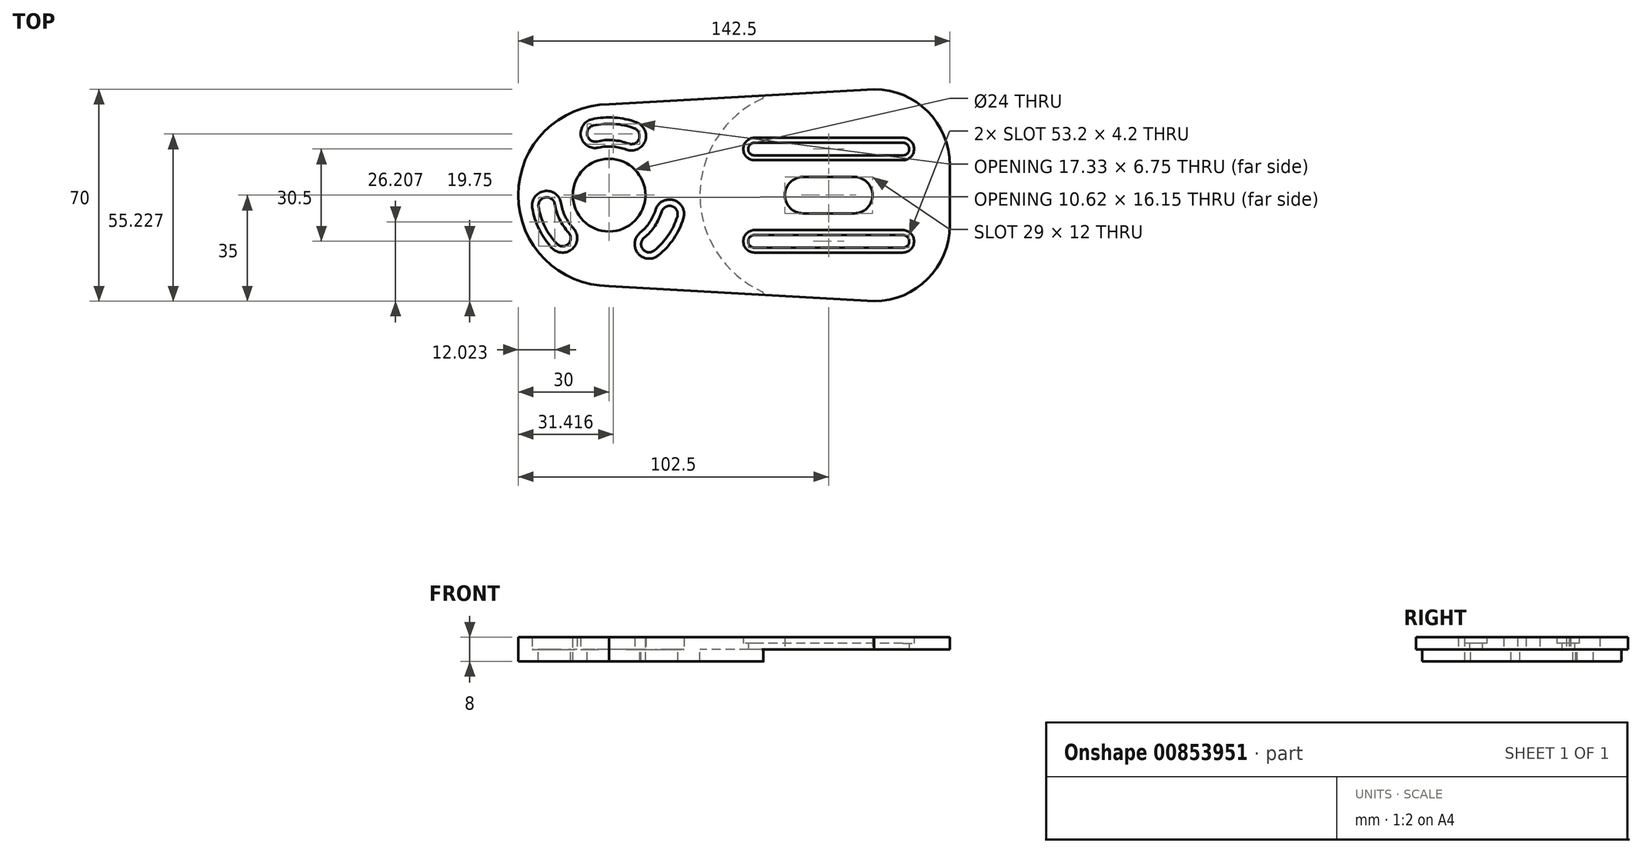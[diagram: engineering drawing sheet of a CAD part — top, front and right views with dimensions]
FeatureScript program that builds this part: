
annotation { "Feature Type Name" : "Feature", "Feature Type Description" : "" }
export const myFeature = defineFeature(function(context is Context, id is Id, definition is map)
    precondition{}
    {
        {
            var Q0;
            Q0=qCreatedBy(makeId("Top.planeOp"),FACE);
            var sketch = newSketch(context, id + "F0", { "sketchPlane" : qUnion([Q0])});
            skLineSegment(sketch, "E0.bottom", {"start": v(39.15, 35) * mm, "end": v(-48.35, 35) * mm, "construction": true});
            skLineSegment(sketch, "E0.top", {"start": v(39.15, -35) * mm, "end": v(-48.35, -35) * mm, "construction": true});
            skLineSegment(sketch, "E0.left", {"start": v(64.15, 10) * mm, "end": v(64.15, -10) * mm});
            skCircle(sketch, "E1", {"center": v(-48.35, 0) * mm, "radius": 12 * mm});
            skArc(sketch, "E2.filletArc", {"start": v(64.15, 10) * mm, "mid": v(56.83, 27.68) * mm, "end": v(39.15, 35) * mm});
            skArc(sketch, "E3.filletArc", {"start": v(39.15, -35) * mm, "mid": v(56.83, -27.68) * mm, "end": v(64.15, -10) * mm});
            skLineSegment(sketch, "E4.bottom", {"start": v(32.65, 6) * mm, "end": v(24.15, 6) * mm});
            skPoint(sketch, "E4.middle", {"position": v(24.15, 0) * mm});
            skLineSegment(sketch, "E5", {"start": v(-48.35, 0) * mm, "end": v(-47.08, 18.16) * mm, "construction": true});
            skPoint(sketch, "E6", {"position": v(64.15, 0) * mm});
            skArc(sketch, "E7", {"start": v(-54, 25.07) * mm, "mid": v(-57.62, 19.34) * mm, "end": v(-51.88, 15.7) * mm});
            skArc(sketch, "E8", {"start": v(-53.53, 23.02) * mm, "mid": v(-55.57, 19.8) * mm, "end": v(-52.35, 17.76) * mm});
            skArc(sketch, "E9", {"start": v(-41.92, 17.03) * mm, "mid": v(-38.44, 18.6) * mm, "end": v(-40.01, 22.08) * mm});
            skArc(sketch, "E10.trimOffspring", {"start": v(-42.66, 15.06) * mm, "mid": v(-47.23, 16.06) * mm, "end": v(-51.88, 15.7) * mm});
            skArc(sketch, "E11.trimOffspring", {"start": v(-41.92, 17.03) * mm, "mid": v(-47.08, 18.16) * mm, "end": v(-52.35, 17.76) * mm});
            skArc(sketch, "E12.trimOffspring", {"start": v(-40.01, 22.08) * mm, "mid": v(-46.7, 23.54) * mm, "end": v(-53.53, 23.02) * mm});
            skArc(sketch, "E13.trimOffspring", {"start": v(-39.27, 24.04) * mm, "mid": v(-46.56, 25.64) * mm, "end": v(-54, 25.07) * mm});
            skArc(sketch, "E14.trimOffspring", {"start": v(-42.66, 15.06) * mm, "mid": v(-36.48, 17.86) * mm, "end": v(-39.27, 24.04) * mm});
            skCircle(sketch, "E15", {"center": v(-48.35, 0) * mm, "radius": 20.9 * mm, "construction": true});
            skLineSegment(sketch, "E16", {"start": v(32.65, 0) * mm, "end": v(24.15, 0) * mm, "construction": true});
            skArc(sketch, "E17", {"start": v(32.65, -6) * mm, "mid": v(38.65, 0) * mm, "end": v(32.65, 6) * mm});
            skLineSegment(sketch, "E18", {"start": v(24.15, 0) * mm, "end": v(24.15, 6) * mm, "construction": true});
            skLineSegment(sketch, "E19.MirrorCS", {"start": v(32.65, -6) * mm, "end": v(24.15, -6) * mm});
            skLineSegment(sketch, "E20.MirrorCS", {"start": v(15.65, 6) * mm, "end": v(24.15, 6) * mm});
            skArc(sketch, "E21.MirrorCS", {"start": v(15.65, -6) * mm, "mid": v(9.65, 0) * mm, "end": v(15.65, 6) * mm});
            skLineSegment(sketch, "E22.MirrorCS", {"start": v(15.65, -6) * mm, "end": v(24.15, -6) * mm});
            skArc(sketch, "E23", {"start": v(-0.35, -11.55) * mm, "mid": v(-4.05, -15.25) * mm, "end": v(-0.35, -18.95) * mm});
            skArc(sketch, "E24", {"start": v(-0.35, -13.15) * mm, "mid": v(-2.45, -15.25) * mm, "end": v(-0.35, -17.35) * mm});
            skLineSegment(sketch, "E25", {"start": v(-0.35, -11.55) * mm, "end": v(24.15, -11.55) * mm});
            skLineSegment(sketch, "E26", {"start": v(-0.35, -15.25) * mm, "end": v(24.15, -15.25) * mm, "construction": true});
            skLineSegment(sketch, "E27", {"start": v(-0.35, -13.15) * mm, "end": v(24.15, -13.15) * mm});
            skLineSegment(sketch, "E28.MirrorCS", {"start": v(-0.35, -17.35) * mm, "end": v(24.15, -17.35) * mm});
            skLineSegment(sketch, "E29.MirrorCS", {"start": v(-0.35, -18.95) * mm, "end": v(24.15, -18.95) * mm});
            skLineSegment(sketch, "E30.MirrorCS", {"start": v(48.65, -11.55) * mm, "end": v(24.15, -11.55) * mm});
            skLineSegment(sketch, "E31.MirrorCS", {"start": v(48.65, -13.15) * mm, "end": v(24.15, -13.15) * mm});
            skLineSegment(sketch, "E32.MirrorCS", {"start": v(48.65, -17.35) * mm, "end": v(24.15, -17.35) * mm});
            skLineSegment(sketch, "E33.MirrorCS", {"start": v(48.65, -18.95) * mm, "end": v(24.15, -18.95) * mm});
            skArc(sketch, "E34.MirrorCS", {"start": v(48.65, -13.15) * mm, "mid": v(50.75, -15.25) * mm, "end": v(48.65, -17.35) * mm});
            skArc(sketch, "E35.MirrorCS", {"start": v(48.65, -11.55) * mm, "mid": v(52.35, -15.25) * mm, "end": v(48.65, -18.95) * mm});
            skLineSegment(sketch, "E36.MirrorCS", {"start": v(-0.35, 11.55) * mm, "end": v(24.15, 11.55) * mm});
            skArc(sketch, "E37.MirrorCS", {"start": v(-0.35, 11.55) * mm, "mid": v(-4.05, 15.25) * mm, "end": v(-0.35, 18.95) * mm});
            skArc(sketch, "E38.MirrorCS", {"start": v(-0.35, 13.15) * mm, "mid": v(-2.45, 15.25) * mm, "end": v(-0.35, 17.35) * mm});
            skLineSegment(sketch, "E39.MirrorCS", {"start": v(-0.35, 13.15) * mm, "end": v(24.15, 13.15) * mm});
            skLineSegment(sketch, "E40.MirrorCS", {"start": v(-0.35, 17.35) * mm, "end": v(24.15, 17.35) * mm});
            skLineSegment(sketch, "E41.MirrorCS", {"start": v(-0.35, 18.95) * mm, "end": v(24.15, 18.95) * mm});
            skLineSegment(sketch, "E42.MirrorCS", {"start": v(48.65, 18.95) * mm, "end": v(24.15, 18.95) * mm});
            skLineSegment(sketch, "E43.MirrorCS", {"start": v(48.65, 17.35) * mm, "end": v(24.15, 17.35) * mm});
            skLineSegment(sketch, "E44.MirrorCS", {"start": v(48.65, 13.15) * mm, "end": v(24.15, 13.15) * mm});
            skLineSegment(sketch, "E45.MirrorCS", {"start": v(48.65, 11.55) * mm, "end": v(24.15, 11.55) * mm});
            skArc(sketch, "E46.MirrorCS", {"start": v(48.65, 11.55) * mm, "mid": v(52.35, 15.25) * mm, "end": v(48.65, 18.95) * mm});
            skArc(sketch, "E47.MirrorCS", {"start": v(48.65, 13.15) * mm, "mid": v(50.75, 15.25) * mm, "end": v(48.65, 17.35) * mm});
            skLineSegment(sketch, "E48", {"start": v(-48.35, 0) * mm, "end": v(-48.35, -30) * mm, "construction": true});
            skLineSegment(sketch, "E49.MirrorCS", {"start": v(-48.35, 0) * mm, "end": v(-48.35, 30) * mm, "construction": true});
            skLineSegment(sketch, "E50", {"start": v(39.15, 35) * mm, "end": v(-48.35, 30) * mm});
            skLineSegment(sketch, "E51", {"start": v(39.15, -35) * mm, "end": v(-48.35, -30) * mm});
            skArc(sketch, "E52", {"start": v(-48.35, 30) * mm, "mid": v(-78.35, 0) * mm, "end": v(-48.35, -30) * mm});
            skArc(sketch, "E53.1.0", {"start": v(-73.71, -4.16) * mm, "mid": v(-71.45, -11.27) * mm, "end": v(-67.24, -17.42) * mm});
            skArc(sketch, "E53.1.1", {"start": v(-67.24, -17.42) * mm, "mid": v(-60.46, -17.7) * mm, "end": v(-60.19, -10.92) * mm});
            skArc(sketch, "E53.1.2", {"start": v(-65.7, -16) * mm, "mid": v(-61.88, -16.15) * mm, "end": v(-61.73, -12.34) * mm});
            skArc(sketch, "E53.1.3", {"start": v(-64.24, -2.6) * mm, "mid": v(-62.82, -7.06) * mm, "end": v(-60.19, -10.92) * mm});
            skArc(sketch, "E53.1.4", {"start": v(-66.3, -2.95) * mm, "mid": v(-64.7, -7.98) * mm, "end": v(-61.73, -12.34) * mm});
            skArc(sketch, "E53.1.5", {"start": v(-71.64, -3.82) * mm, "mid": v(-69.56, -10.35) * mm, "end": v(-65.7, -16) * mm});
            skArc(sketch, "E53.1.6", {"start": v(-64.24, -2.6) * mm, "mid": v(-69.75, 1.35) * mm, "end": v(-73.71, -4.16) * mm});
            skArc(sketch, "E53.1.7", {"start": v(-66.3, -2.95) * mm, "mid": v(-69.41, -0.72) * mm, "end": v(-71.64, -3.82) * mm});
            skArc(sketch, "E53.2.0", {"start": v(-32.07, -19.88) * mm, "mid": v(-27.04, -14.37) * mm, "end": v(-23.81, -7.65) * mm});
            skArc(sketch, "E53.2.1", {"start": v(-23.81, -7.65) * mm, "mid": v(-26.97, -1.64) * mm, "end": v(-32.98, -4.8) * mm});
            skArc(sketch, "E53.2.2", {"start": v(-25.82, -7.02) * mm, "mid": v(-27.6, -3.64) * mm, "end": v(-30.97, -5.42) * mm});
            skArc(sketch, "E53.2.3", {"start": v(-38.15, -12.46) * mm, "mid": v(-35, -9) * mm, "end": v(-32.98, -4.8) * mm});
            skArc(sketch, "E53.2.4", {"start": v(-36.82, -14.08) * mm, "mid": v(-33.26, -10.18) * mm, "end": v(-30.97, -5.42) * mm});
            skArc(sketch, "E53.2.5", {"start": v(-33.4, -18.26) * mm, "mid": v(-28.78, -13.2) * mm, "end": v(-25.82, -7.02) * mm});
            skArc(sketch, "E53.2.6", {"start": v(-38.15, -12.46) * mm, "mid": v(-38.82, -19.21) * mm, "end": v(-32.07, -19.88) * mm});
            skArc(sketch, "E53.2.7", {"start": v(-36.82, -14.08) * mm, "mid": v(-37.2, -17.88) * mm, "end": v(-33.4, -18.26) * mm});
            skLineSegment(sketch, "E54", {"start": v(64.15, 0) * mm, "end": v(-78.35, 0) * mm, "construction": true});
            skLineSegment(sketch, "E55", {"start": v(-18.35, 0) * mm, "end": v(-18.35, 31.71) * mm, "construction": true});
            skLineSegment(sketch, "E56.MirrorCS", {"start": v(-18.35, 0) * mm, "end": v(-18.35, -31.71) * mm, "construction": true});
            skArc(sketch, "E57", {"start": v(-18.35, 0) * mm, "mid": v(-11.88, -20.28) * mm, "end": v(5.15, -33.06) * mm});
            skArc(sketch, "E58.MirrorCS", {"start": v(-18.35, 0) * mm, "mid": v(-11.88, 20.28) * mm, "end": v(5.15, 33.06) * mm});
            skSolve(sketch);
        }
        {
            var Q0;
            Q0=makeQuery(id+"F0.imprint","IMPRINT",FACE,{"disambiguationData":[TD([[makeQuery(id+"F0.imprint","IMPRINT",EDGE,{"derivedFrom":sQuery(id+"F0.wireOp",EDGE,"E1")}),-1.0]])]});
            var Q1;
            Q1=makeQuery(id+"F0.imprint","IMPRINT",FACE,{"disambiguationData":[TD([[makeQuery(id+"F0.imprint","IMPRINT",EDGE,{"derivedFrom":sQuery(id+"F0.wireOp",EDGE,"E7")}),1.0]])]});
            var Q2;
            Q2=makeQuery(id+"F0.imprint","IMPRINT",FACE,{"disambiguationData":[TD([[makeQuery(id+"F0.imprint","IMPRINT",EDGE,{"derivedFrom":sQuery(id+"F0.wireOp",EDGE,"E53.1.0")}),1.0]])]});
            var Q3;
            Q3=makeQuery(id+"F0.imprint","IMPRINT",FACE,{"disambiguationData":[TD([[makeQuery(id+"F0.imprint","IMPRINT",EDGE,{"derivedFrom":sQuery(id+"F0.wireOp",EDGE,"E53.2.0")}),1.0]])]});
            var Q4;
            {var subQ0=sQuery(id+"F0.wireOp",EDGE,"E56.MirrorCS");Q4=makeQuery(id+"F0.imprint","IMPRINT",FACE,{"disambiguationData":[TD([[makeQuery(id+"F0.imprint","IMPRINT",EDGE,{"derivedFrom":subQ0}),1.0]])]});}
            var Q5;
            {var subQ0=sQuery(id+"F0.wireOp",EDGE,"E55");Q5=makeQuery(id+"F0.imprint","IMPRINT",FACE,{"disambiguationData":[TD([[makeQuery(id+"F0.imprint","IMPRINT",EDGE,{"derivedFrom":subQ0}),-1.0]])]});}
            extrude(context, id + "F1", {"entities" : qUnion([Q0, Q1, Q2, Q3, Q4, Q5]), "oppositeDirection" : true, "depth" : 4 * mm, "offsetDistance" : 25 * mm});
        }
        {
            var Q0;
            Q0=qSketchRegion(id+"F0",true);
            extrude(context, id + "F2", {"entities" : qUnion([Q0]), "operationType" : NewBodyOperationType.ADD, "depth" : 4 * mm, "offsetDistance" : 25 * mm});
        }
        {
            var Q0;
            Q0=makeQuery(id+"F0.imprint","IMPRINT",FACE,{"disambiguationData":[TD([[makeQuery(id+"F0.imprint","IMPRINT",EDGE,{"derivedFrom":sQuery(id+"F0.wireOp",EDGE,"E23")}),1.0]])]});
            var Q1;
            Q1=makeQuery(id+"F0.imprint","IMPRINT",FACE,{"disambiguationData":[TD([[makeQuery(id+"F0.imprint","IMPRINT",EDGE,{"derivedFrom":sQuery(id+"F0.wireOp",EDGE,"E36.MirrorCS")}),1.0]])]});
            extrude(context, id + "F3", {"entities" : qUnion([Q0, Q1]), "operationType" : NewBodyOperationType.ADD, "depth" : 2 * mm, "offsetDistance" : 25 * mm});
        }
        {
            var Q0;
            Q0=makeQuery(id+"F1.opExtrude","SWEPT_EDGE",EDGE,{"disambiguationData":[OSD([sQuery(id+"F0.wireOp",EDGE,"E51"),sQuery(id+"F0.wireOp",EDGE,"E57")])]});
            var Q1;
            Q1=makeQuery(id+"F1.opExtrude","SWEPT_EDGE",EDGE,{"disambiguationData":[OSD([sQuery(id+"F0.wireOp",EDGE,"E50"),sQuery(id+"F0.wireOp",EDGE,"E58.MirrorCS")])]});
            fillet(context, id + "F4", {"entities" : qUnion([Q0, Q1]), "radius" : 0.5 * mm, "tangentPropagation" : true, "allowEdgeOverflow" : false});
        }
    });
